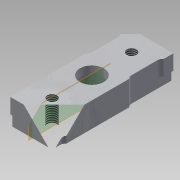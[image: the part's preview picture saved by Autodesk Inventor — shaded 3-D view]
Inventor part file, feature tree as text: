
AUTODESK INVENTOR PART (.ipt)
format: ipt  version: 2016 (Build 200138000, 138)  size: 214,016 bytes
history: native  units: mm
features: extrude x7, sketch x6, reference x4, thread x2, plane x1, mirror x1
ambient origin geometry x8: Origin, YZ Plane, XZ Plane, XY Plane, X Axis, Y Axis, Z Axis, Center Point
bodies: Solid1 (feature_tree)
feature tree (21):
  extrude  "Extrusion1"  Depth=15.0mm
  extrude  "Extrusion2"  Depth=4.0mm TaperAngle=0.0deg
  extrude  "Extrusion3"  Depth=2.4mm
  sketch  "Sketch6"  dims[d6=2.4mm d7=2.4mm]
  sketch  "Sketch7"  dims[d8=5.0mm d9=5.0mm]
  extrude  "Extrusion8"  Depth=5.0mm
  extrude  "Extrusion9"  Depth=0.5mm
  plane  "Work Plane1"
  mirror  "Mirror1"
  extrude  "Extrusion10"  Depth=3.0mm
  extrude  "Extrusion11"  Depth=4.0mm
  thread  "Thread1"  [1 undecoded]
  thread  "Thread2"  [1 undecoded]
  reference  "Reference1"
  sketch  "Sketch2"  dims[d0=5.5mm d1=15.0mm]
  reference  "Reference2"
  sketch  "Sketch3"  dims[d2=2.0mm d3=0.0mm d4=4.0mm d5=0.0mm]
  reference  "Reference3"
  reference  "Reference4"
  sketch  "Sketch8"  dims[d10=10.0mm d11=0.0mm d16=0.5mm d17=0.5mm]
  sketch  "Sketch9"  dims[d21=4.0mm d23=3.0mm d25=4.0mm d29=3.0mm d30=2.0mm d33=100.0mm d34=0.0mm d35=2.2mm d36=0.0mm d37=-5.5mm d38=10.0mm d39=3.5mm d40=0.5mm d41=1.5mm d42=0.2mm d43=0.0mm d44=6.0mm d45=100.0mm d46=0.0mm d47=10.0mm d48=0.0mm d49=10.0mm d50=0.0mm d51=0.5mm]
note: 2 required parameter values undecoded (feature->parameter linkage not recoverable at this tier; creation-order binding heuristic only, values carry confidence <= 0.55)
